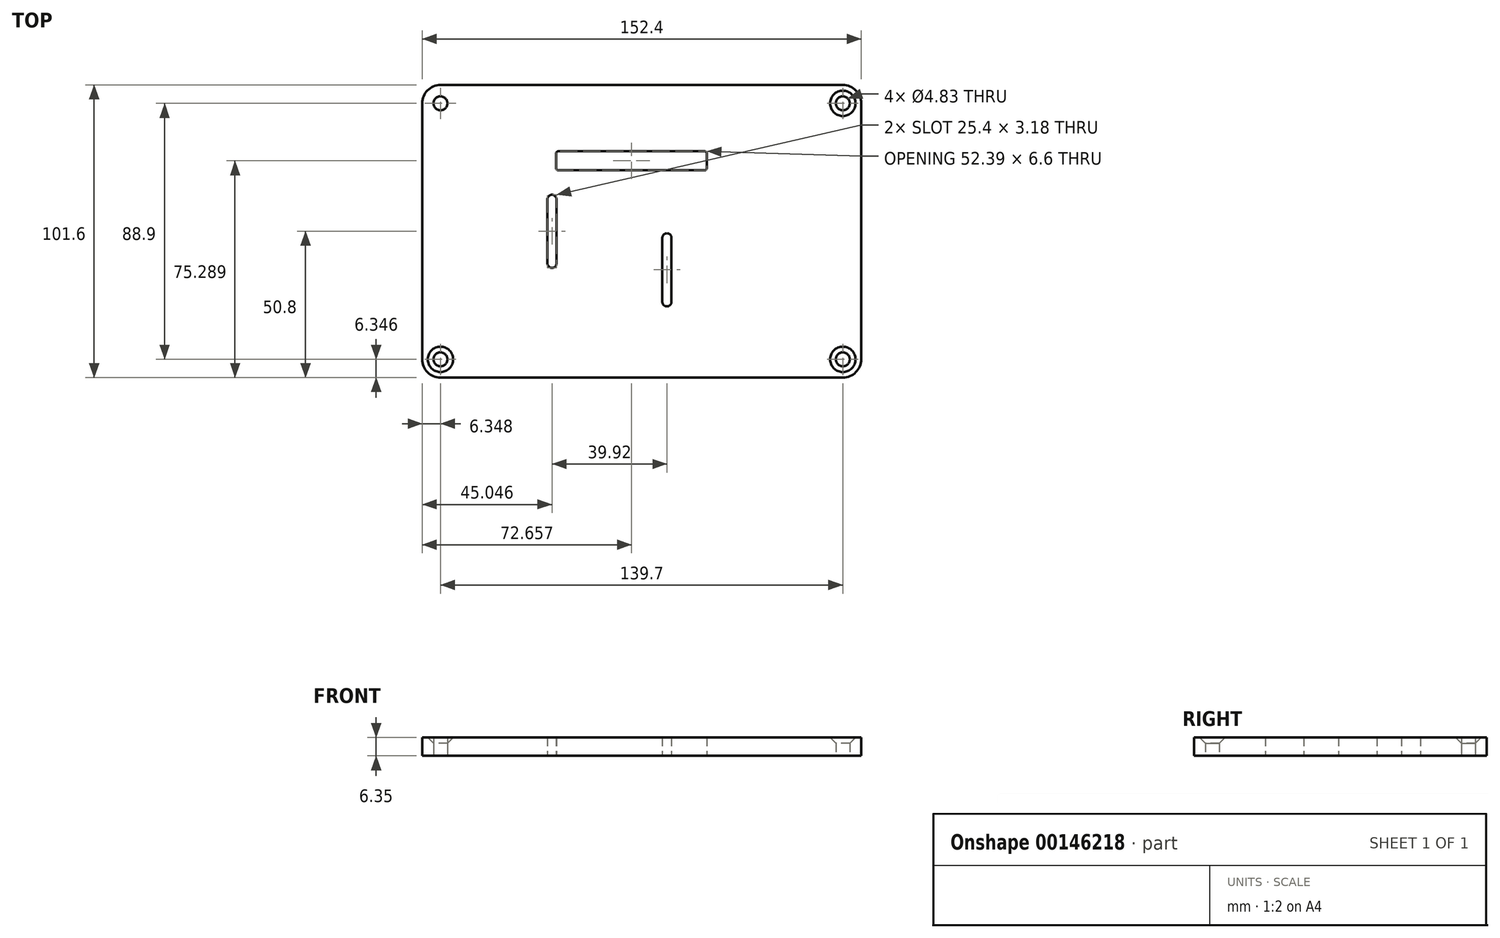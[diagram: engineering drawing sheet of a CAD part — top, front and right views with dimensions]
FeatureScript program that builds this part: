
annotation { "Feature Type Name" : "Feature", "Feature Type Description" : "" }
export const myFeature = defineFeature(function(context is Context, id is Id, definition is map)
    precondition{}
    {
        {
            var Q0;
            Q0=qCreatedBy(makeId("Top.planeOp"),FACE);
            var sketch = newSketch(context, id + "F0", { "sketchPlane" : qUnion([Q0])});
            skLineSegment(sketch, "E0.bottom", {"start": v(-66.1, -50.8) * mm, "end": v(73.6, -50.8) * mm});
            skLineSegment(sketch, "E0.top", {"start": v(-66.1, 50.8) * mm, "end": v(73.6, 50.8) * mm});
            skLineSegment(sketch, "E0.left", {"start": v(-72.45, -44.45) * mm, "end": v(-72.45, 44.45) * mm});
            skLineSegment(sketch, "E0.right", {"start": v(79.95, -44.45) * mm, "end": v(79.95, 44.45) * mm});
            skPoint(sketch, "E1.visualSharp", {"position": v(-72.45, 50.8) * mm});
            skArc(sketch, "E1.filletArc", {"start": v(-66.1, 50.8) * mm, "mid": v(-70.6, 48.94) * mm, "end": v(-72.45, 44.45) * mm});
            skPoint(sketch, "E2.visualSharp", {"position": v(-72.45, -50.8) * mm});
            skArc(sketch, "E2.filletArc", {"start": v(-72.45, -44.45) * mm, "mid": v(-70.6, -48.94) * mm, "end": v(-66.1, -50.8) * mm});
            skPoint(sketch, "E3.visualSharp", {"position": v(79.95, 50.8) * mm});
            skArc(sketch, "E3.filletArc", {"start": v(79.95, 44.45) * mm, "mid": v(78.09, 48.94) * mm, "end": v(73.6, 50.8) * mm});
            skPoint(sketch, "E4.visualSharp", {"position": v(79.95, -50.8) * mm});
            skArc(sketch, "E4.filletArc", {"start": v(73.6, -50.8) * mm, "mid": v(78.09, -48.94) * mm, "end": v(79.95, -44.45) * mm});
            skCircle(sketch, "E5", {"center": v(-66.1, 44.45) * mm, "radius": 2.41 * mm});
            skCircle(sketch, "E6.MirrorC", {"center": v(-66.1, -44.45) * mm, "radius": 2.41 * mm});
            skCircle(sketch, "E7.MirrorC", {"center": v(73.6, 44.45) * mm, "radius": 2.41 * mm});
            skCircle(sketch, "E8.MirrorC", {"center": v(73.6, -44.45) * mm, "radius": 2.41 * mm});
            skLineSegment(sketch, "E9.bottom", {"start": v(-25.2, 27.8) * mm, "end": v(25.6, 27.8) * mm});
            skLineSegment(sketch, "E9.top", {"start": v(-25.2, 21.19) * mm, "end": v(25.6, 21.19) * mm});
            skLineSegment(sketch, "E9.left", {"start": v(-25.99, 27) * mm, "end": v(-25.99, 21.98) * mm});
            skLineSegment(sketch, "E9.right", {"start": v(26.4, 27) * mm, "end": v(26.4, 21.98) * mm});
            skPoint(sketch, "E9.middle", {"position": v(0.2, 24.49) * mm});
            skPoint(sketch, "E10.visualSharp", {"position": v(-25.99, 27.8) * mm});
            skArc(sketch, "E10.filletArc", {"start": v(-25.2, 27.8) * mm, "mid": v(-25.75, 27.56) * mm, "end": v(-25.99, 27) * mm});
            skPoint(sketch, "E11.visualSharp", {"position": v(-25.99, 21.19) * mm});
            skArc(sketch, "E11.filletArc", {"start": v(-25.99, 21.98) * mm, "mid": v(-25.75, 21.42) * mm, "end": v(-25.2, 21.19) * mm});
            skPoint(sketch, "E12.visualSharp", {"position": v(26.4, 21.19) * mm});
            skArc(sketch, "E12.filletArc", {"start": v(25.6, 21.19) * mm, "mid": v(26.17, 21.42) * mm, "end": v(26.4, 21.98) * mm});
            skPoint(sketch, "E13.visualSharp", {"position": v(26.4, 27.8) * mm});
            skArc(sketch, "E13.filletArc", {"start": v(26.4, 27) * mm, "mid": v(26.17, 27.56) * mm, "end": v(25.6, 27.8) * mm});
            skPoint(sketch, "E14.middle", {"position": v(-27.4, 0) * mm});
            skLineSegment(sketch, "E15.left", {"start": v(-25.82, 11.11) * mm, "end": v(-25.82, -11.11) * mm});
            skLineSegment(sketch, "E15.right", {"start": v(-29, 11.11) * mm, "end": v(-29, -11.11) * mm});
            skArc(sketch, "E16", {"start": v(-25.82, 11.11) * mm, "mid": v(-27.4, 12.7) * mm, "end": v(-29, 11.11) * mm});
            skArc(sketch, "E17", {"start": v(-29, -11.11) * mm, "mid": v(-27.4, -12.7) * mm, "end": v(-25.82, -11.11) * mm});
            skPoint(sketch, "E18.middle", {"position": v(12.52, -13.38) * mm});
            skLineSegment(sketch, "E19.left", {"start": v(14.1, -2.28) * mm, "end": v(14.1, -24.5) * mm});
            skLineSegment(sketch, "E19.right", {"start": v(10.93, -2.26) * mm, "end": v(10.93, -24.49) * mm});
            skArc(sketch, "E20", {"start": v(14.1, -2.28) * mm, "mid": v(12.52, -0.68) * mm, "end": v(10.93, -2.26) * mm});
            skArc(sketch, "E21", {"start": v(10.93, -24.49) * mm, "mid": v(12.5, -26.08) * mm, "end": v(14.1, -24.5) * mm});
            skSolve(sketch);
        }
        {
            var Q0;
            Q0 = qSketchRegion(id + "F0", true);
            extrude(context, id + "F1", {"entities" : qUnion([Q0]), "depth" : 6.35 * mm});
        }
        {
            var Q0;
            Q0=makeQuery(id+"F1.opExtrude","CAP_EDGE",EDGE,{"disambiguationData":[OSD([sQuery(id+"F0.wireOp",EDGE,"E6.MirrorC")])],"isStart":false});
            var Q1;
            Q1=makeQuery(id+"F1.opExtrude","CAP_EDGE",EDGE,{"disambiguationData":[OSD([sQuery(id+"F0.wireOp",EDGE,"E8.MirrorC")])],"isStart":false});
            var Q2;
            Q2=makeQuery(id+"F1.opExtrude","CAP_EDGE",EDGE,{"disambiguationData":[OSD([sQuery(id+"F0.wireOp",EDGE,"E7.MirrorC")])],"isStart":false});
            var Q3;
            Q3=makeQuery(id+"F1.opExtrude","CAP_EDGE",EDGE,{"disambiguationData":[OSD([sQuery(id+"F0.wireOp",EDGE,"E5")])],"isStart":false});
            chamfer(context, id + "F2", {"entities" : qUnion([Q0, Q1, Q2, Q3]), "width" : 1.98 * mm, "tangentPropagation" : true});
        }
    });
